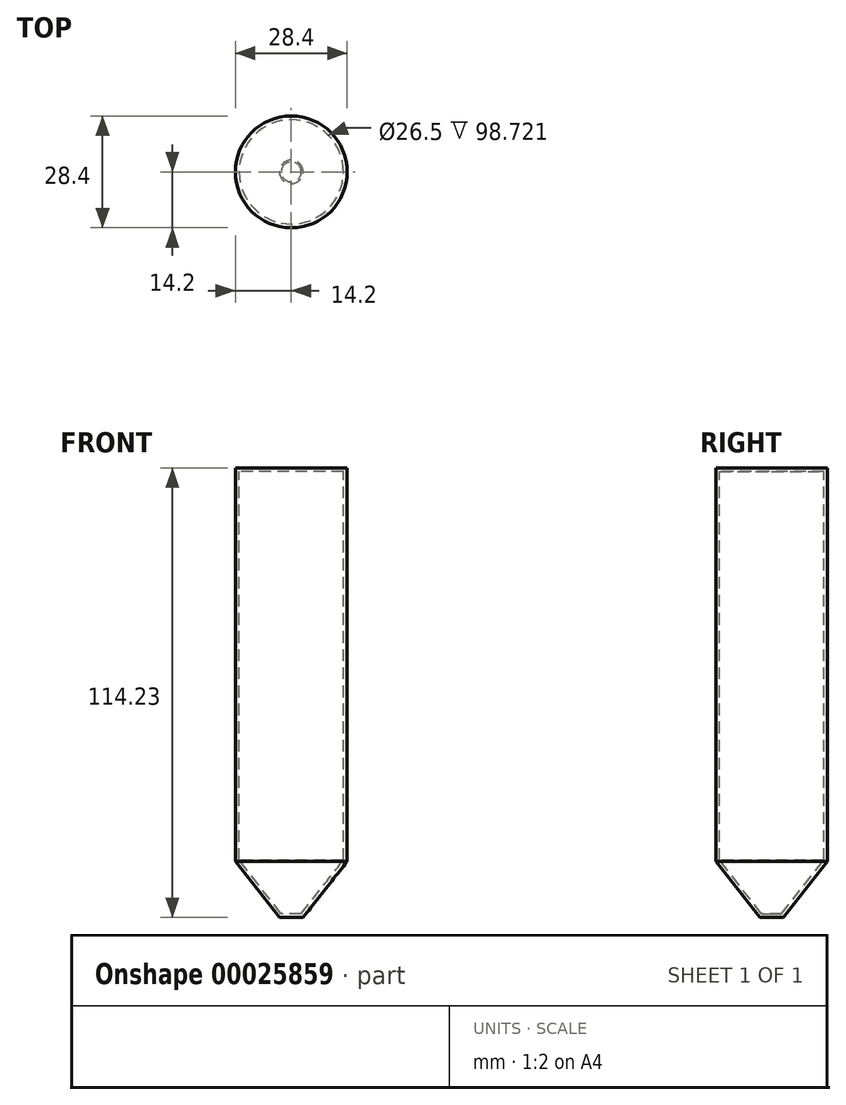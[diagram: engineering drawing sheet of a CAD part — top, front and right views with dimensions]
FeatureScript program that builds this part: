
annotation { "Feature Type Name" : "Feature", "Feature Type Description" : "" }
export const myFeature = defineFeature(function(context is Context, id is Id, definition is map)
    precondition{}
    {
        {
            var Q0;
            Q0=qCreatedBy(makeId("Front.planeOp"),FACE);
            var sketch = newSketch(context, id + "F0", { "sketchPlane" : qUnion([Q0])});
            skLineSegment(sketch, "E0", {"start": v(0, 60.92) * mm, "end": v(0, -53.31) * mm, "construction": true});
            skLineSegment(sketch, "E1", {"start": v(0, -53.31) * mm, "end": v(3, -53.31) * mm});
            skLineSegment(sketch, "E2", {"start": v(0, 60.92) * mm, "end": v(14.2, 60.92) * mm});
            skLineSegment(sketch, "E3", {"start": v(14.2, 60.92) * mm, "end": v(14.2, -39.08) * mm});
            skLineSegment(sketch, "E4", {"start": v(14.2, -39.08) * mm, "end": v(3, -53.31) * mm});
            skLineSegment(sketch, "E5.0", {"start": v(0, -52.36) * mm, "end": v(2.54, -52.36) * mm});
            skLineSegment(sketch, "E5.1", {"start": v(13.25, -38.75) * mm, "end": v(2.54, -52.36) * mm});
            skLineSegment(sketch, "E5.2", {"start": v(13.25, 59.97) * mm, "end": v(13.25, -38.75) * mm});
            skLineSegment(sketch, "E5.3", {"start": v(0, 59.97) * mm, "end": v(13.25, 59.97) * mm});
            skLineSegment(sketch, "E6", {"start": v(0, 59.97) * mm, "end": v(0, 60.92) * mm});
            skLineSegment(sketch, "E7", {"start": v(0, -52.36) * mm, "end": v(0, -53.31) * mm});
            skSolve(sketch);
        }
        {
            var Q0;
            Q0 = qSketchRegion(id + "F0", true);
            var Q1;
            Q1=sQuery(id+"F0.wireOp",EDGE,"E0");
            revolve(context, id + "F1", {"entities" : qUnion([Q0]), "axis" : qUnion([Q1]), "revolveType" : RevolveType.FULL});
        }
    });
